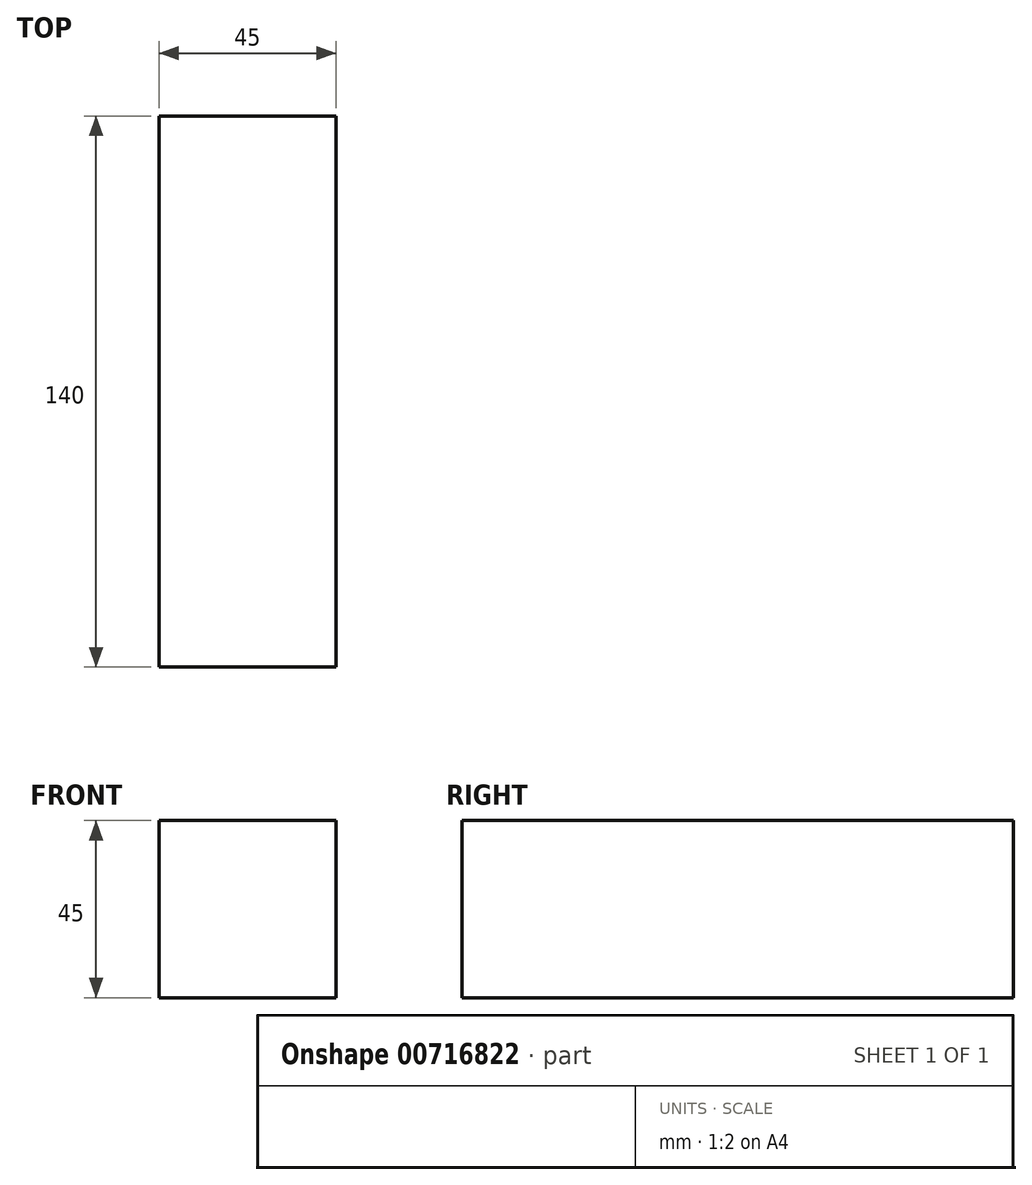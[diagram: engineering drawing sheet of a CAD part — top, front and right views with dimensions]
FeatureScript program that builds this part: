
annotation { "Feature Type Name" : "Feature", "Feature Type Description" : "" }
export const myFeature = defineFeature(function(context is Context, id is Id, definition is map)
    precondition{}
    {
        {
            var Q0;
            Q0=qCreatedBy(makeId("Front.planeOp"),FACE);
            var sketch = newSketch(context, id + "F0", { "sketchPlane" : qUnion([Q0])});
            skLineSegment(sketch, "E0.bottom", {"start": v(22.5, 22.5) * mm, "end": v(-22.5, 22.5) * mm});
            skLineSegment(sketch, "E0.top", {"start": v(22.5, -22.5) * mm, "end": v(-22.5, -22.5) * mm});
            skLineSegment(sketch, "E0.left", {"start": v(22.5, 22.5) * mm, "end": v(22.5, -22.5) * mm});
            skLineSegment(sketch, "E0.right", {"start": v(-22.5, 22.5) * mm, "end": v(-22.5, -22.5) * mm});
            skPoint(sketch, "E0.middle", {"position": v(0, 0) * mm});
            skSolve(sketch);
        }
        {
            var Q0;
            Q0 = qSketchRegion(id + "F0", true);
            extrude(context, id + "F1", {"entities" : qUnion([Q0]), "endBound" : BoundingType.SYMMETRIC, "depth" : 140 * mm, "offsetDistance" : 25 * mm});
        }
    });
